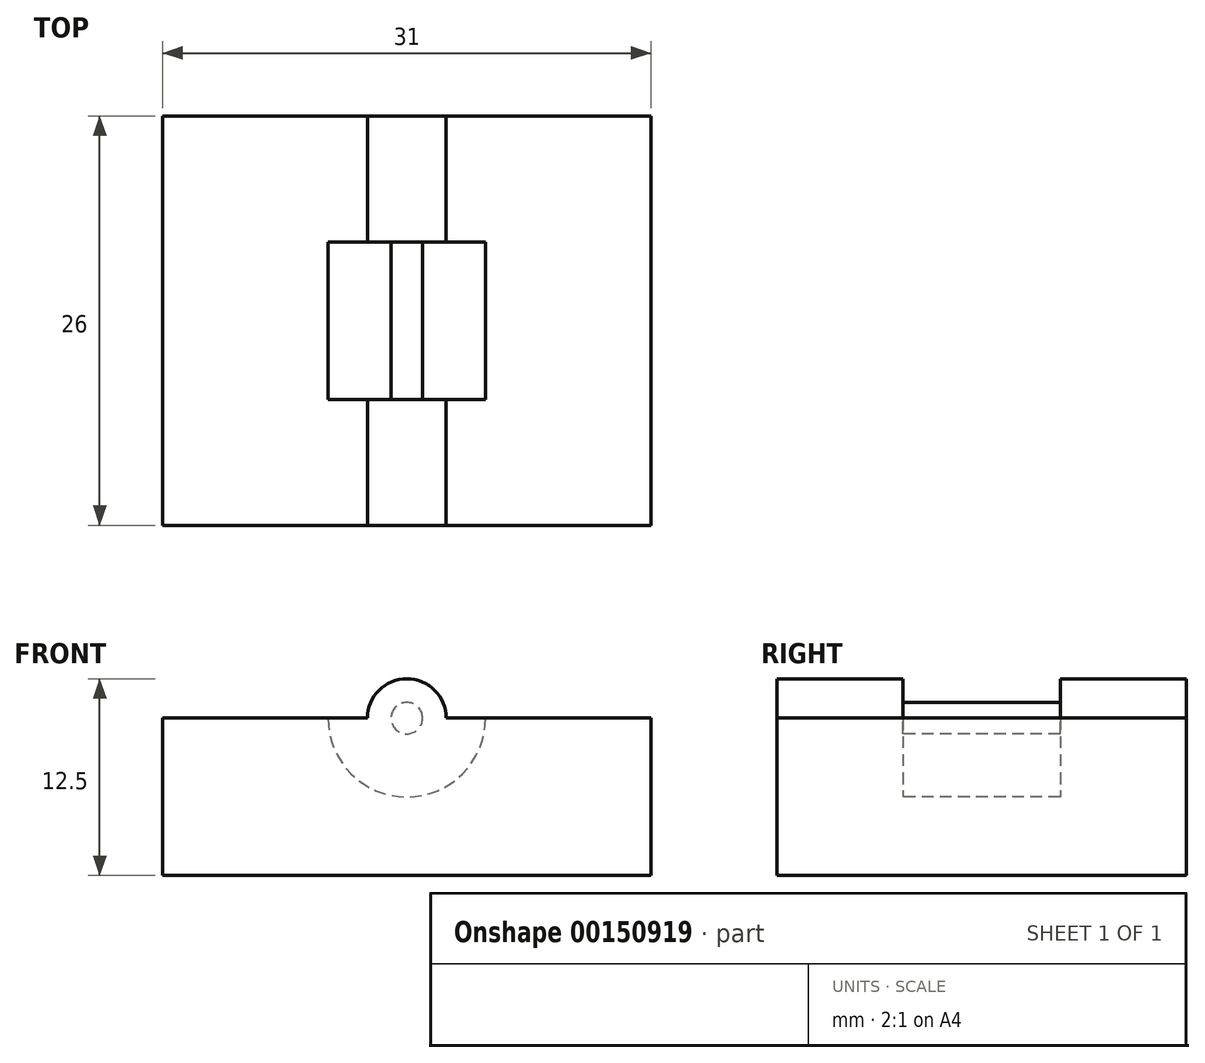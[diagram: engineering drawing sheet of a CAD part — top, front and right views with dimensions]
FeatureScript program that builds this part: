
annotation { "Feature Type Name" : "Feature", "Feature Type Description" : "" }
export const myFeature = defineFeature(function(context is Context, id is Id, definition is map)
    precondition{}
    {
        {
            var Q0;
            Q0=qCreatedBy(makeId("Front.planeOp"),FACE);
            var sketch = newSketch(context, id + "F0", { "sketchPlane" : qUnion([Q0])});
            skLineSegment(sketch, "E0.bottom", {"start": v(0, 0) * mm, "end": v(31, 0) * mm});
            skLineSegment(sketch, "E0.top", {"start": v(0, 10) * mm, "end": v(31, 10) * mm});
            skLineSegment(sketch, "E0.left", {"start": v(0, 0) * mm, "end": v(0, 10) * mm});
            skLineSegment(sketch, "E0.right", {"start": v(31, 0) * mm, "end": v(31, 10) * mm});
            skSolve(sketch);
        }
        {
            var Q0;
            Q0 = qSketchRegion(id + "F0", true);
            extrude(context, id + "F1", {"entities" : qUnion([Q0]), "endBound" : BoundingType.SYMMETRIC, "depth" : 26 * mm});
        }
        {
            var Q0;
            Q0=makeQuery(id+"F1.opExtrude","CAP_FACE",FACE,{"disambiguationData":[OSD([sQuery(id+"F0.wireOp",EDGE,"E0.bottom"),sQuery(id+"F0.wireOp",EDGE,"E0.top"),sQuery(id+"F0.wireOp",EDGE,"E0.left"),sQuery(id+"F0.wireOp",EDGE,"E0.right")])],"isStart":false});
            var sketch = newSketch(context, id + "F2", { "sketchPlane" : qUnion([Q0])});
            skCircle(sketch, "E1", {"center": v(15.5, 10) * mm, "radius": 1 * mm});
            skSolve(sketch);
        }
        {
            var Q0;
            Q0 = qSketchRegion(id + "F2", true);
            extrude(context, id + "F3", {"entities" : qUnion([Q0]), "operationType" : NewBodyOperationType.ADD, "oppositeDirection" : true, "depth" : 20 * mm});
        }
        {
            var Q0;
            Q0=makeQuery(id+"F3.boolean.opBoolean","MERGE",FACE,{"derivedFrom":[makeQuery(id+"F1.opExtrude","CAP_FACE",FACE,{"disambiguationData":[OSD([sQuery(id+"F0.wireOp",EDGE,"E0.bottom"),sQuery(id+"F0.wireOp",EDGE,"E0.top"),sQuery(id+"F0.wireOp",EDGE,"E0.left"),sQuery(id+"F0.wireOp",EDGE,"E0.right")])],"isStart":false}),makeQuery(id+"F3.opExtrude","CAP_FACE",FACE,{"disambiguationData":[OSD([sQuery(id+"F2.wireOp",EDGE,"E1")])],"isStart":true})]});
            var sketch = newSketch(context, id + "F4", { "sketchPlane" : qUnion([Q0])});
            skCircle(sketch, "E2", {"center": v(15.5, 10) * mm, "radius": 2.5 * mm});
            skSolve(sketch);
        }
        {
            var Q0;
            Q0 = qSketchRegion(id + "F4", true);
            extrude(context, id + "F5", {"entities" : qUnion([Q0]), "operationType" : NewBodyOperationType.ADD, "oppositeDirection" : true, "depth" : 10 * mm});
        }
        {
            var Q0;
            Q0=makeQuery(id+"F1.opExtrude","CAP_FACE",FACE,{"disambiguationData":[OSD([sQuery(id+"F0.wireOp",EDGE,"E0.bottom"),sQuery(id+"F0.wireOp",EDGE,"E0.top"),sQuery(id+"F0.wireOp",EDGE,"E0.left"),sQuery(id+"F0.wireOp",EDGE,"E0.right")])],"isStart":true});
            var sketch = newSketch(context, id + "F6", { "sketchPlane" : qUnion([Q0])});
            skCircle(sketch, "E3", {"center": v(-15.5, 10) * mm, "radius": 2.5 * mm});
            skSolve(sketch);
        }
        {
            var Q0;
            Q0 = qSketchRegion(id + "F6", true);
            extrude(context, id + "F7", {"entities" : qUnion([Q0]), "operationType" : NewBodyOperationType.ADD, "oppositeDirection" : true, "depth" : 10 * mm});
        }
        {
            var Q0;
            Q0=qCreatedBy(makeId("Front.planeOp"),FACE);
            var sketch = newSketch(context, id + "F8", { "sketchPlane" : qUnion([Q0])});
            skCircle(sketch, "E4", {"center": v(15.5, 10) * mm, "radius": 1 * mm});
            skCircle(sketch, "E5", {"center": v(15.5, 10) * mm, "radius": 5 * mm});
            skSolve(sketch);
        }
        {
            var Q0;
            Q0 = qSketchRegion(id + "F8", true);
            extrude(context, id + "F9", {"entities" : qUnion([Q0]), "operationType" : NewBodyOperationType.REMOVE, "endBound" : BoundingType.SYMMETRIC, "oppositeDirection" : true, "depth" : 10 * mm});
        }
    });
